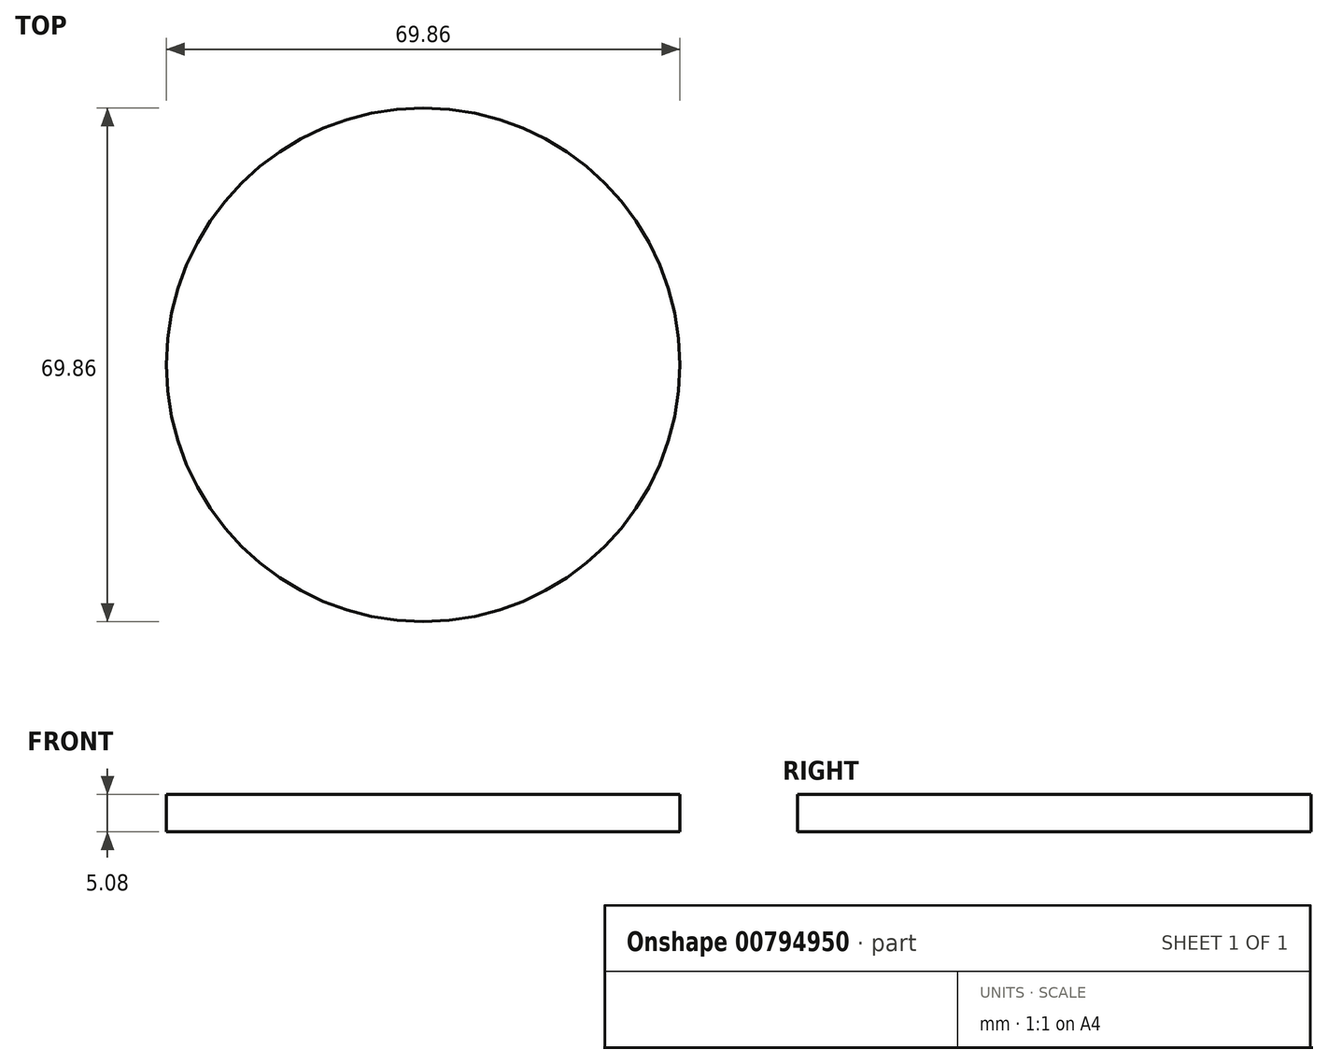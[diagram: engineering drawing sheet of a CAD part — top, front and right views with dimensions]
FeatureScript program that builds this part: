
annotation { "Feature Type Name" : "Feature", "Feature Type Description" : "" }
export const myFeature = defineFeature(function(context is Context, id is Id, definition is map)
    precondition{}
    {
        {
            var Q0;
            Q0=qCreatedBy(makeId("Top.planeOp"),FACE);
            var sketch = newSketch(context, id + "F0", { "sketchPlane" : qUnion([Q0])});
            skCircle(sketch, "E0", {"center": v(0, 0) * mm, "radius": 34.93 * mm});
            skCircle(sketch, "E1", {"center": v(0, 0) * mm, "radius": 36.83 * mm});
            skSolve(sketch);
        }
        {
            var Q0;
            Q0=qCreatedBy(makeId("Front.planeOp"),FACE);
            var sketch = newSketch(context, id + "F1", { "sketchPlane" : qUnion([Q0])});
            skLineSegment(sketch, "E2", {"start": v(0, -162.56) * mm, "end": v(0, 0) * mm});
            skSolve(sketch);
        }
        {
            var Q0;
            Q0=qCreatedBy(makeId("Front.planeOp"),FACE);
            var sketch = newSketch(context, id + "F2", { "sketchPlane" : qUnion([Q0])});
            skLineSegment(sketch, "E3.MirrorCS", {"start": v(-50.27, 162) * mm, "end": v(-36.83, 0) * mm});
            skLineSegment(sketch, "E4.MirrorCS", {"start": v(-48.36, 162) * mm, "end": v(-34.92, 0) * mm});
            skSolve(sketch);
        }
        {
            var Q0;
            Q0=qCreatedBy(makeId("Front.planeOp"),FACE);
            var sketch = newSketch(context, id + "F3", { "sketchPlane" : qUnion([Q0])});
            skLineSegment(sketch, "E5", {"start": v(-50.27, 162) * mm, "end": v(-50.52, 163.1) * mm});
            skLineSegment(sketch, "E6", {"start": v(-36.82, 0) * mm, "end": v(-34.94, 0) * mm});
            skLineSegment(sketch, "E7", {"start": v(-48.36, 162) * mm, "end": v(-48.6, 163.07) * mm});
            skLineSegment(sketch, "E8", {"start": v(-50.52, 182.14) * mm, "end": v(-50.52, 163.1) * mm});
            skLineSegment(sketch, "E9", {"start": v(-48.6, 182.14) * mm, "end": v(-48.6, 163.07) * mm});
            skLineSegment(sketch, "E10", {"start": v(-50.52, 182.14) * mm, "end": v(-48.6, 182.14) * mm});
            skSolve(sketch);
        }
        {
            var Q0;
            Q0=sQuery(id+"F2.wireOp",EDGE,"E4.MirrorCS");
            var Q1;
            Q1=sQuery(id+"F3.wireOp",EDGE,"E9");
            var Q2;
            Q2=sQuery(id+"F3.wireOp",EDGE,"E7");
            var Q3;
            Q3=sQuery(id+"F2.wireOp",EDGE,"E3.MirrorCS");
            var Q4;
            Q4=sQuery(id+"F3.wireOp",EDGE,"E10");
            var Q5;
            Q5=sQuery(id+"F3.wireOp",EDGE,"E5");
            var Q6;
            Q6=sQuery(id+"F3.wireOp",EDGE,"E8");
            var Q7;
            Q7=sQuery(id+"F3.wireOp",EDGE,"E6");
            var Q8;
            Q8=sQuery(id+"F1.wireOp",EDGE,"E2");
            revolve(context, id + "F4", {"bodyType" : ToolBodyType.SURFACE, "surfaceOperationType" : NewSurfaceOperationType.NEW, "surfaceEntities" : qUnion([Q0, Q1, Q2, Q3, Q4, Q5, Q6, Q7]), "axis" : qUnion([Q8]), "revolveType" : RevolveType.FULL});
        }
        {
            var Q0;
            Q0=makeQuery(id+"F0.imprint","IMPRINT",FACE,{"disambiguationData":[TD([[makeQuery(id+"F0.imprint","IMPRINT",EDGE,{"derivedFrom":sQuery(id+"F0.wireOp",EDGE,"E0")}),1.0]])]});
            extrude(context, id + "F5", {"entities" : qUnion([Q0]), "oppositeDirection" : true, "depth" : 5.08 * mm, "offsetDistance" : 25.4 * mm});
        }
    });
